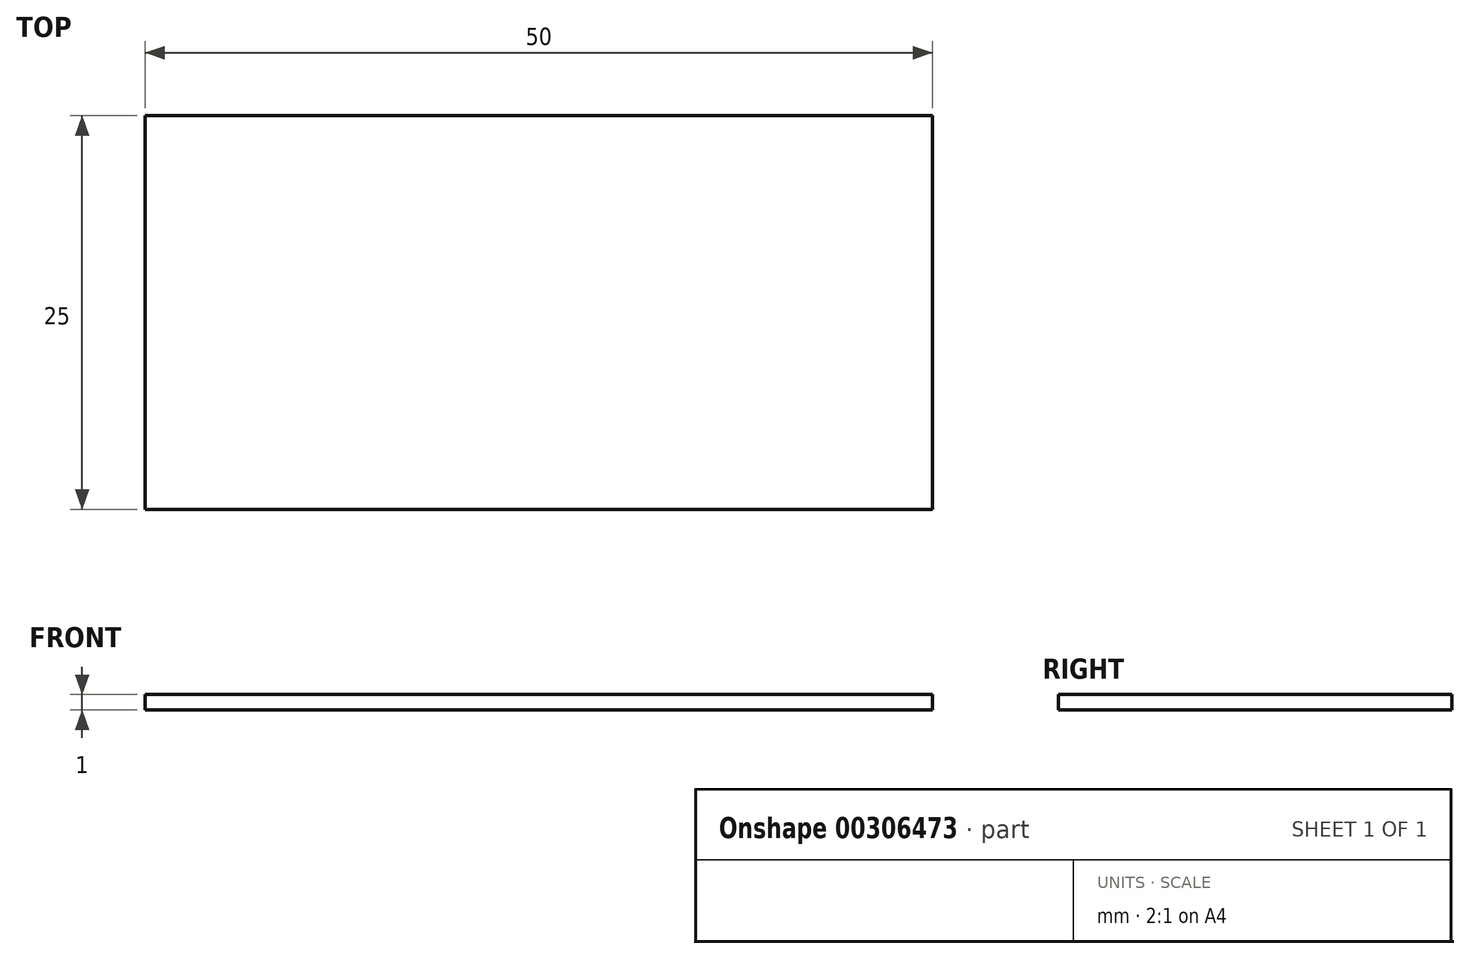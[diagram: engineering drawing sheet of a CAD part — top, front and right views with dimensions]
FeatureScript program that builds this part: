
annotation { "Feature Type Name" : "Feature", "Feature Type Description" : "" }
export const myFeature = defineFeature(function(context is Context, id is Id, definition is map)
    precondition{}
    {
        {
            var Q0;
            Q0=qCreatedBy(makeId("Top.planeOp"),FACE);
            var sketch = newSketch(context, id + "F0", { "sketchPlane" : qUnion([Q0])});
            skLineSegment(sketch, "E0.bottom", {"start": v(0, 0) * mm, "end": v(-100, 0) * mm});
            skLineSegment(sketch, "E0.top", {"start": v(0, 50) * mm, "end": v(-100, 50) * mm});
            skLineSegment(sketch, "E0.left", {"start": v(0, 0) * mm, "end": v(0, 50) * mm});
            skLineSegment(sketch, "E0.right", {"start": v(-100, 0) * mm, "end": v(-100, 50) * mm});
            skSolve(sketch);
        }
        {
            var Q0;
            Q0=makeQuery(id+"F0.imprint","IMPRINT",FACE,{"disambiguationData":[TD([[makeQuery(id+"F0.imprint","IMPRINT",EDGE,{"derivedFrom":sQuery(id+"F0.wireOp",EDGE,"E0.bottom")}),-1.0]])]});
            extrude(context, id + "F1", {"entities" : qUnion([Q0]), "depth" : 2 * mm});
        }
        {
            var Q0;
            Q0=makeQuery(id+"F1.opExtrude","SWEPT_BODY",BODY,{"disambiguationData":[OSD([sQuery(id+"F0.wireOp",EDGE,"E0.bottom"),sQuery(id+"F0.wireOp",EDGE,"E0.top"),sQuery(id+"F0.wireOp",EDGE,"E0.left"),sQuery(id+"F0.wireOp",EDGE,"E0.right")])]});
            var Q1;
            Q1=qCreatedBy(makeId("Origin.pointOp"),VERTEX);
            transform(context, id + "F2", {"entities" : qUnion([Q0]), "transformType" : TransformType.SCALE_UNIFORMLY, "scale" : 0.5, "scalePoint" : qUnion([Q1]), "makeCopy" : false});
        }
    });
